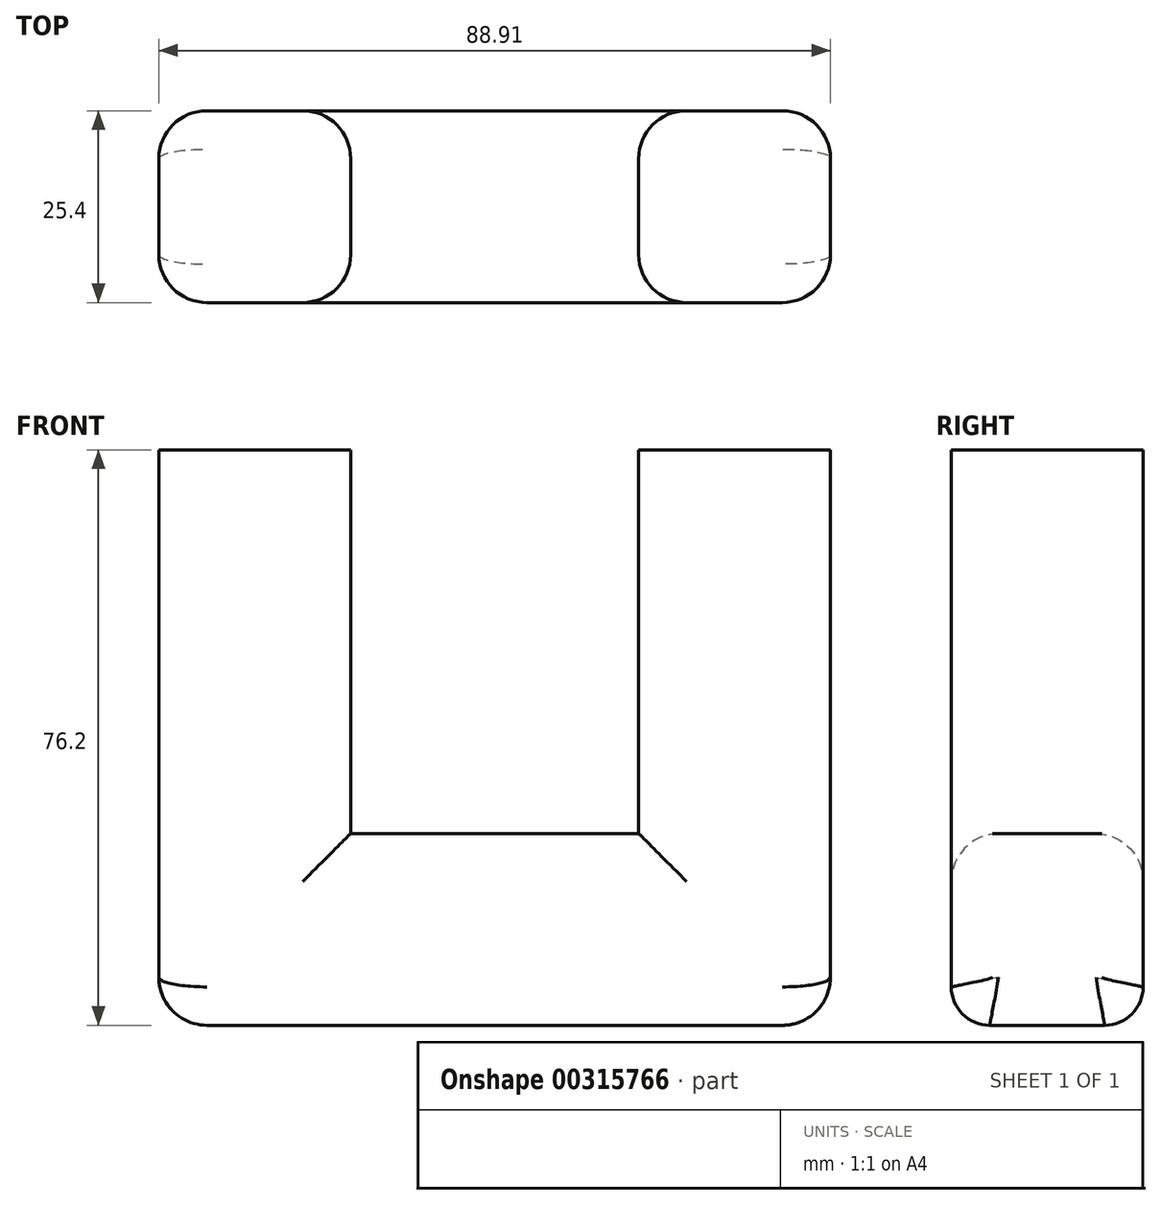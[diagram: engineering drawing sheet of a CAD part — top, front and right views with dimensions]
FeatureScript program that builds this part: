
annotation { "Feature Type Name" : "Feature", "Feature Type Description" : "" }
export const myFeature = defineFeature(function(context is Context, id is Id, definition is map)
    precondition{}
    {
        {
            var Q0;
            Q0=qCreatedBy(makeId("Front.planeOp"),FACE);
            var sketch = newSketch(context, id + "F0", { "sketchPlane" : qUnion([Q0])});
            skLineSegment(sketch, "E0.bottom", {"start": v(-48.18, 50.8) * mm, "end": v(-22.78, 50.8) * mm});
            skLineSegment(sketch, "E0.top", {"start": v(-48.18, 0) * mm, "end": v(-22.78, 0) * mm});
            skLineSegment(sketch, "E0.left", {"start": v(-48.18, 50.8) * mm, "end": v(-48.18, 0) * mm});
            skLineSegment(sketch, "E0.right", {"start": v(-22.78, 50.8) * mm, "end": v(-22.78, 0) * mm});
            skLineSegment(sketch, "E1.bottom", {"start": v(15.33, 50.8) * mm, "end": v(40.73, 50.8) * mm});
            skLineSegment(sketch, "E1.top", {"start": v(15.33, 0) * mm, "end": v(40.73, 0) * mm});
            skLineSegment(sketch, "E1.left", {"start": v(15.33, 50.8) * mm, "end": v(15.33, 0) * mm});
            skLineSegment(sketch, "E1.right", {"start": v(40.73, 50.8) * mm, "end": v(40.73, 0) * mm});
            skLineSegment(sketch, "E2.bottom", {"start": v(-48.18, 0) * mm, "end": v(40.72, 0) * mm});
            skLineSegment(sketch, "E2.top", {"start": v(-48.18, -25.4) * mm, "end": v(40.72, -25.4) * mm});
            skLineSegment(sketch, "E2.left", {"start": v(-48.18, 0) * mm, "end": v(-48.18, -25.4) * mm});
            skLineSegment(sketch, "E2.right", {"start": v(40.72, 0) * mm, "end": v(40.72, -25.4) * mm});
            skSolve(sketch);
        }
        {
            var Q0;
            Q0=makeQuery(id+"F0.imprint","IMPRINT",FACE,{"disambiguationData":[TD([[makeQuery(id+"F0.imprint","IMPRINT",EDGE,{"derivedFrom":sQuery(id+"F0.wireOp",EDGE,"E2.top")}),1.0]])]});
            var Q1;
            Q1=makeQuery(id+"F0.imprint","IMPRINT",FACE,{"disambiguationData":[TD([[makeQuery(id+"F0.imprint","IMPRINT",EDGE,{"derivedFrom":sQuery(id+"F0.wireOp",EDGE,"E1.bottom")}),-1.0]])]});
            var Q2;
            Q2=makeQuery(id+"F0.imprint","IMPRINT",FACE,{"disambiguationData":[TD([[makeQuery(id+"F0.imprint","IMPRINT",EDGE,{"derivedFrom":sQuery(id+"F0.wireOp",EDGE,"E0.bottom")}),-1.0]])]});
            extrude(context, id + "F1", {"entities" : qUnion([Q0, Q1, Q2]), "depth" : 25.4 * mm});
        }
        {
            var Q0;
            Q0=makeQuery(id+"F1.opExtrude","CAP_EDGE",EDGE,{"disambiguationData":[OSD([sQuery(id+"F0.wireOp",EDGE,"E1.right")])],"isStart":false});
            var Q1;
            Q1=makeQuery(id+"F1.opExtrude","CAP_EDGE",EDGE,{"disambiguationData":[OSD([sQuery(id+"F0.wireOp",EDGE,"E1.right")])],"isStart":true});
            var Q2;
            Q2=makeQuery(id+"F1.opExtrude","CAP_EDGE",EDGE,{"disambiguationData":[OSD([sQuery(id+"F0.wireOp",EDGE,"E1.left")])],"isStart":true});
            var Q3;
            Q3=makeQuery(id+"F1.opExtrude","CAP_EDGE",EDGE,{"disambiguationData":[OSD([sQuery(id+"F0.wireOp",EDGE,"E1.left")])],"isStart":false});
            var Q4;
            Q4=makeQuery(id+"F1.opExtrude","CAP_EDGE",EDGE,{"disambiguationData":[OSD([sQuery(id+"F0.wireOp",EDGE,"E0.right")])],"isStart":false});
            var Q5;
            Q5=makeQuery(id+"F1.opExtrude","CAP_EDGE",EDGE,{"disambiguationData":[OSD([sQuery(id+"F0.wireOp",EDGE,"E0.left"),sQuery(id+"F0.wireOp",EDGE,"E2.left")])],"isStart":false});
            var Q6;
            Q6=makeQuery(id+"F1.opExtrude","CAP_EDGE",EDGE,{"disambiguationData":[OSD([sQuery(id+"F0.wireOp",EDGE,"E0.left"),sQuery(id+"F0.wireOp",EDGE,"E2.left")])],"isStart":true});
            var Q7;
            Q7=makeQuery(id+"F1.opExtrude","CAP_EDGE",EDGE,{"disambiguationData":[OSD([sQuery(id+"F0.wireOp",EDGE,"E0.right")])],"isStart":true});
            var Q8;
            Q8=makeQuery(id+"F1.opExtrude","SWEPT_EDGE",EDGE,{"disambiguationData":[OSD([sQuery(id+"F0.wireOp",EDGE,"E2.top"),sQuery(id+"F0.wireOp",EDGE,"E2.left")])]});
            var Q9;
            Q9=makeQuery(id+"F1.opExtrude","SWEPT_EDGE",EDGE,{"disambiguationData":[OSD([sQuery(id+"F0.wireOp",EDGE,"E2.top"),sQuery(id+"F0.wireOp",EDGE,"E2.right")])]});
            var Q10;
            Q10=makeQuery(id+"F1.opExtrude","CAP_EDGE",EDGE,{"disambiguationData":[OSD([sQuery(id+"F0.wireOp",EDGE,"E2.bottom")])],"isStart":false});
            var Q11;
            Q11=makeQuery(id+"F1.opExtrude","CAP_EDGE",EDGE,{"disambiguationData":[OSD([sQuery(id+"F0.wireOp",EDGE,"E2.bottom")])],"isStart":true});
            fillet(context, id + "F2", {"entities" : qUnion([Q0, Q1, Q2, Q3, Q4, Q5, Q6, Q7, Q8, Q9, Q10, Q11]), "radius" : 6.35 * mm, "tangentPropagation" : true, "allowEdgeOverflow" : false});
        }
        {
            var Q0;
            Q0=makeQuery(id+"F1.opExtrude","CAP_EDGE",EDGE,{"disambiguationData":[OSD([sQuery(id+"F0.wireOp",EDGE,"E2.top")])],"isStart":true});
            var Q1;
            Q1=makeQuery(id+"F1.opExtrude","CAP_EDGE",EDGE,{"disambiguationData":[OSD([sQuery(id+"F0.wireOp",EDGE,"E2.top")])],"isStart":false});
            fillet(context, id + "F3", {"entities" : qUnion([Q0, Q1]), "radius" : 5.08 * mm, "tangentPropagation" : true, "allowEdgeOverflow" : false});
        }
    });
